# Revit family: FU_Inspec_Corso_5-1
name_source: partatom
category: Furniture
units: mm (PartAtom-declared; Revit-internal decimal feet)

## family parameters
Always vertical = Yes
Cut with Voids When Loaded = No
OmniClass Number = 23.40.20.00
OmniClass Title = General Furniture and Specialties
Room Calculation Point = No
Shared = No
Work Plane-Based = No

## types (2) — shared parameters
Assembly Code = E2020
Depth = 900 mm  [stored 2.95276 ft]
Description = Lounge chair on tubular steel frame with rounded rear legs. Upholstered seat and back
Details Material = Leather - Natural
Height = 770 mm  [stored 2.52625 ft]
Keynote = 46.B
Manufacturer = Inspec
Model = Corso 5.1
Supporting Material = Fabric - Canvas - Natural Linen
URL = https://inspecfurniture.com
Weight = 9.5kg
Width = 645 mm  [stored 2.11614 ft]
zero-valued in all types: Default Elevation

## per-type parameters (varying)
| type | Frame Material | Upholstery Material |
| Chrome w Natural Leather Seat | Metal - Chrome - Polished | Leather - Natural |
| White w Natural Linen Seat | Metal - White - Matte | Fabric - Canvas - Natural Linen |

note: [stored X ft] marks values corroborated as IEEE doubles in the binary element streams (Revit-internal decimal feet)

## geometry (parser evidence)
native form markers: Blend x8, Sweep x2
no freeform markers — native parametric forms only
